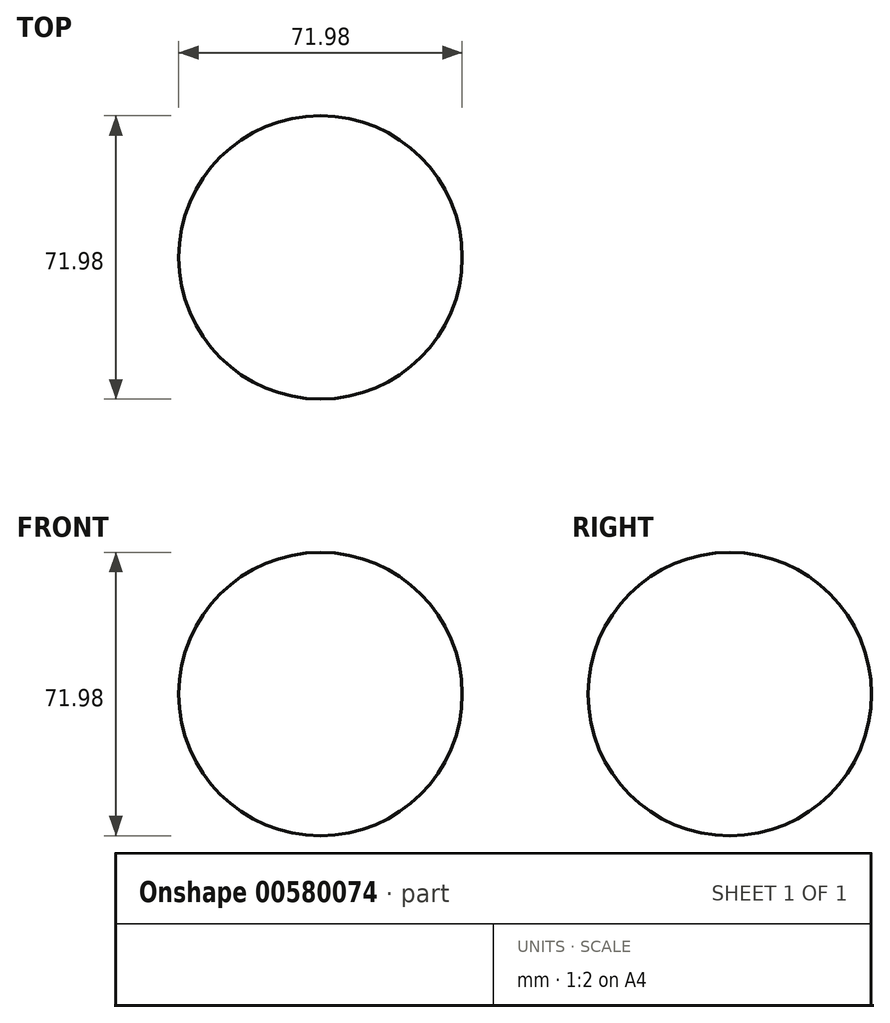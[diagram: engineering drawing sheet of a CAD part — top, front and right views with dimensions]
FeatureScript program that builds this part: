
annotation { "Feature Type Name" : "Feature", "Feature Type Description" : "" }
export const myFeature = defineFeature(function(context is Context, id is Id, definition is map)
    precondition{}
    {
        {
            var Q0;
            Q0=qCreatedBy(makeId("Front.planeOp"),FACE);
            var sketch = newSketch(context, id + "F0", { "sketchPlane" : qUnion([Q0])});
            skCircle(sketch, "E0", {"center": v(0, 0) * mm, "radius": 36 * mm});
            skLineSegment(sketch, "E1", {"start": v(0, 36) * mm, "end": v(0, -36) * mm});
            skSolve(sketch);
        }
        {
            var Q0;
            {var subQ0=sQuery(id+"F0.wireOp",EDGE,"E1");Q0=makeQuery(id+"F0.imprint","IMPRINT",FACE,{"disambiguationData":[TD([[makeQuery(id+"F0.imprint","IMPRINT",EDGE,{"derivedFrom":subQ0}),-1.0]])]});}
            var Q1;
            Q1=sQuery(id+"F0.wireOp",EDGE,"E1");
            revolve(context, id + "F1", {"entities" : qUnion([Q0]), "axis" : qUnion([Q1]), "revolveType" : RevolveType.FULL});
        }
    });
